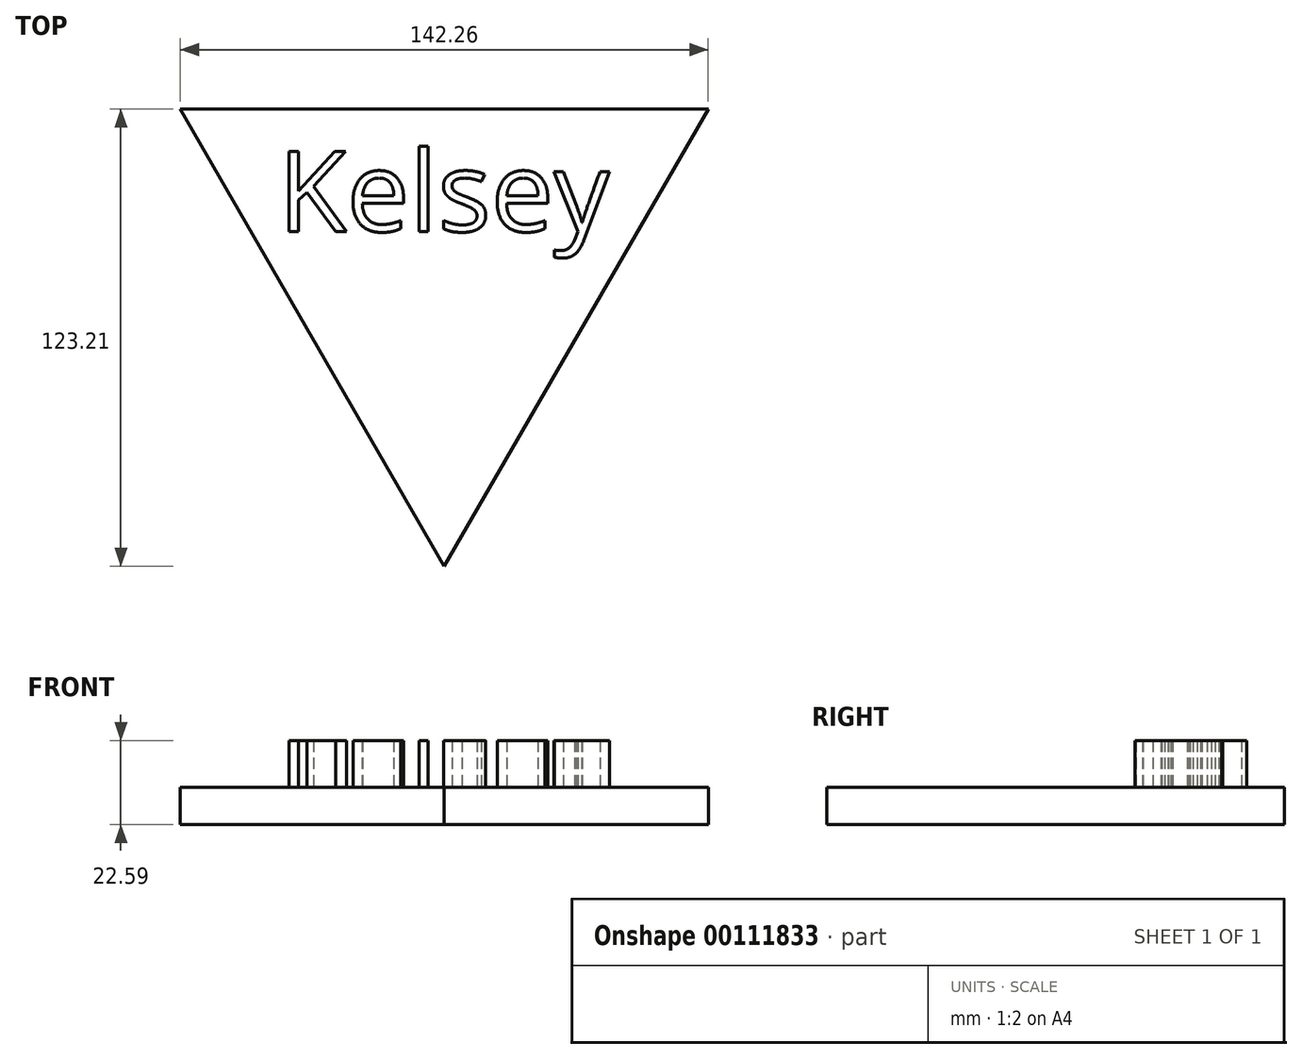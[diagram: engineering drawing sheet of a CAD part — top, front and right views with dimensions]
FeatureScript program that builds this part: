
annotation { "Feature Type Name" : "Feature", "Feature Type Description" : "" }
export const myFeature = defineFeature(function(context is Context, id is Id, definition is map)
    precondition{}
    {
        {
            var Q0;
            Q0=qCreatedBy(makeId("Top.planeOp"),FACE);
            var sketch = newSketch(context, id + "F0", { "sketchPlane" : qUnion([Q0])});
            skCircle(sketch, "E0.cCircle", {"center": v(0, 0) * mm, "radius": 41.07 * mm, "construction": true});
            skLineSegment(sketch, "E0.0", {"start": v(-71.13, 41.07) * mm, "end": v(71.13, 41.07) * mm});
            skLineSegment(sketch, "E0.1", {"start": v(71.13, 41.07) * mm, "end": v(0, -82.14) * mm});
            skLineSegment(sketch, "E0.2", {"start": v(0, -82.14) * mm, "end": v(-71.13, 41.07) * mm});
            skPoint(sketch, "E0.0.midPoint", {"position": v(0, 41.07) * mm});
            skSolve(sketch);
        }
        {
            var Q0;
            Q0=makeQuery(id+"F0.imprint","IMPRINT",FACE,{"disambiguationData":[TD([[makeQuery(id+"F0.imprint","IMPRINT",EDGE,{"derivedFrom":sQuery(id+"F0.wireOp",EDGE,"E0.0")}),-1.0]])]});
            extrude(context, id + "F1", {"entities" : qUnion([Q0]), "depth" : 10.03 * mm});
        }
        {
            var Q0;
            Q0=makeQuery(id+"F1.opExtrude","CAP_FACE",FACE,{"disambiguationData":[OSD([sQuery(id+"F0.wireOp",EDGE,"E0.0"),sQuery(id+"F0.wireOp",EDGE,"E0.1"),sQuery(id+"F0.wireOp",EDGE,"E0.2")])],"isStart":false});
            var sketch = newSketch(context, id + "F2", { "sketchPlane" : qUnion([Q0])});
            skText(sketch, "E1", { "text": "Kelsey", "fontName": "OpenSans-Regular.ttf"});
            const initialGuessF2  = {"E1": [-0.04477, 0.00809, 1, 0, 0.02167]};
            skSetInitialGuess(sketch, initialGuessF2);
            skSolve(sketch);
        }
        {
            var Q0;
            Q0 = qSketchRegion(id + "F2", true);
            extrude(context, id + "F3", {"entities" : qUnion([Q0]), "operationType" : NewBodyOperationType.ADD, "depth" : 12.55 * mm});
        }
    });
